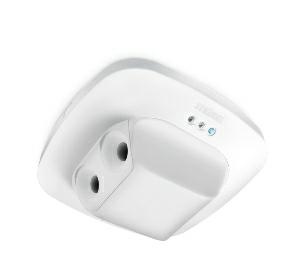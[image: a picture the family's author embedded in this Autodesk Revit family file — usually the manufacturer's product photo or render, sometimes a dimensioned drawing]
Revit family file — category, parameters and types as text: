
# Revit family: dual_us_007850
name_source: partatom
category: Elektroinstallationen
revit_build: Autodesk Revit 2016 (Build: 20190508_0715(x64)
units: mm (PartAtom-declared; Revit-internal decimal feet)

## family parameters
Basisbauteil = Fläche
Beim Laden mit Abzugskörper schneiden = Nein
Bemaßung runder Anschluss = Durchmesser verwenden
Beschriftungsausrichtung beibehalten = Nein
Gemeinsam genutzt = Nein
Raumberechnungspunkt = Nein
Teiletyp = Normal

## types (1)
- Dual US
    Apparent Load = 0 VA
    Beschreibung = Type: Presence detector; Dimensions (L x W x H): 73 x 120 x 120 mm; Mains power supply: 220 – 240 V / 50 – 60 Hz; Sensor Technology: Ultrasonic; Application, place: Indoors; Application, room: corridor / aisle, Indoors; Installation site: ceiling; Installation: Concealed wiring; Electronic scalability: Yes; Mechanical scalability: No; Mounting height: 2,50 – 3,50 m; Optimum mounting height: 2,8 m; Detection angle: 360 °; Sneak-by guard: Yes; Reach, radial: 20 x 3 m (60 m²); Reach, tangential: 20 x 3 m (60 m²); Twilight setting TEACH: Yes; Twilight setting: 10 – 1000 lx; Time setting: 30 sec – 30 min; Constant-lighting control: No; Basic light level function: No; Functions: Normal / test mode, Semi-/fully automatic, Pushbutton / switch mode, Manual ON / ON-OFF; Settings via: Remote control, DIP switches, Potentiometers, Smart Remote; With remote control: Yes; Interconnection: Yes; Type of interconnection: Master/slave, Master/master; IP-rating: IP20; Material: Plastic; Ambient temperature: -25 – 55 °C; Colour: white; Colour, RAL: 9010; Manufacturer's Warranty: 5 years; Version: COM2; PU1, EAN: 4007841007850
    Height = 0 mm  [stored 0 ft]
    Hersteller = Steinel
    Length = 73 mm
    Maximum range = 10.098 m
    ModVariant = Nein
    Modell = 007850
    Mounting Place = Ceiling
    Mounting Type = Recessed
    Number of Poles = 1
    OnlyDefault = Ja
    Power Factor = 1
    Product Name = Dual US
    Product group = Presence detector
    ProductGroupID = 4
    Protection Class = Protection class
    Protection Degree = IP 20
    RlxData = <blob elided: 160557 chars, md5=247edb6a>
    Sensor characteristics = Stretched
    Sensor type = Passive (infrared)
    SensorDataFile = <blob elided: 184890 chars, md5=e609621d>
    Type of entry = Motion
    Typenbild = produkt1_007850.jpg
    Typenkommentare = Product without accessories
    URL = http://relux.com
    VarID = ---
    Voltage = 0 V
    Vorgabe-Ansicht = 1800 mm
    Weight = 0.00 kg
    Width = 120 mm  [stored 0.393701 ft]

note: [stored X ft] marks values corroborated as IEEE doubles in the binary element streams (Revit-internal decimal feet)

## geometry (parser evidence)
native form markers: Sweep x19
no freeform markers — native parametric forms only
